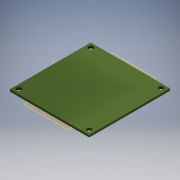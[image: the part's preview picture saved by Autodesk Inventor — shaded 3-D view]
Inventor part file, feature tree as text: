
AUTODESK INVENTOR PART (.ipt)
format: ipt  version: 2016 (Build 200138000, 138)  size: 94,720 bytes
history: native  units: mm
features: plane x1, extrude x1, sketch x1, reference x1
ambient origin geometry x8: Origin, YZ Plane, XZ Plane, XY Plane, X Axis, Y Axis, Z Axis, Center Point
bodies: Solid1 (feature_tree)
feature tree (4):
  plane  "Work Plane1"
  extrude  "Extrusion1"  [1 undecoded]
  sketch  "Sketch1"  dims[d0=1.5mm d1=0.0mm]
  reference  "Reference1"
note: 1 required parameter value undecoded (feature->parameter linkage not recoverable at this tier; creation-order binding heuristic only, values carry confidence <= 0.55)
